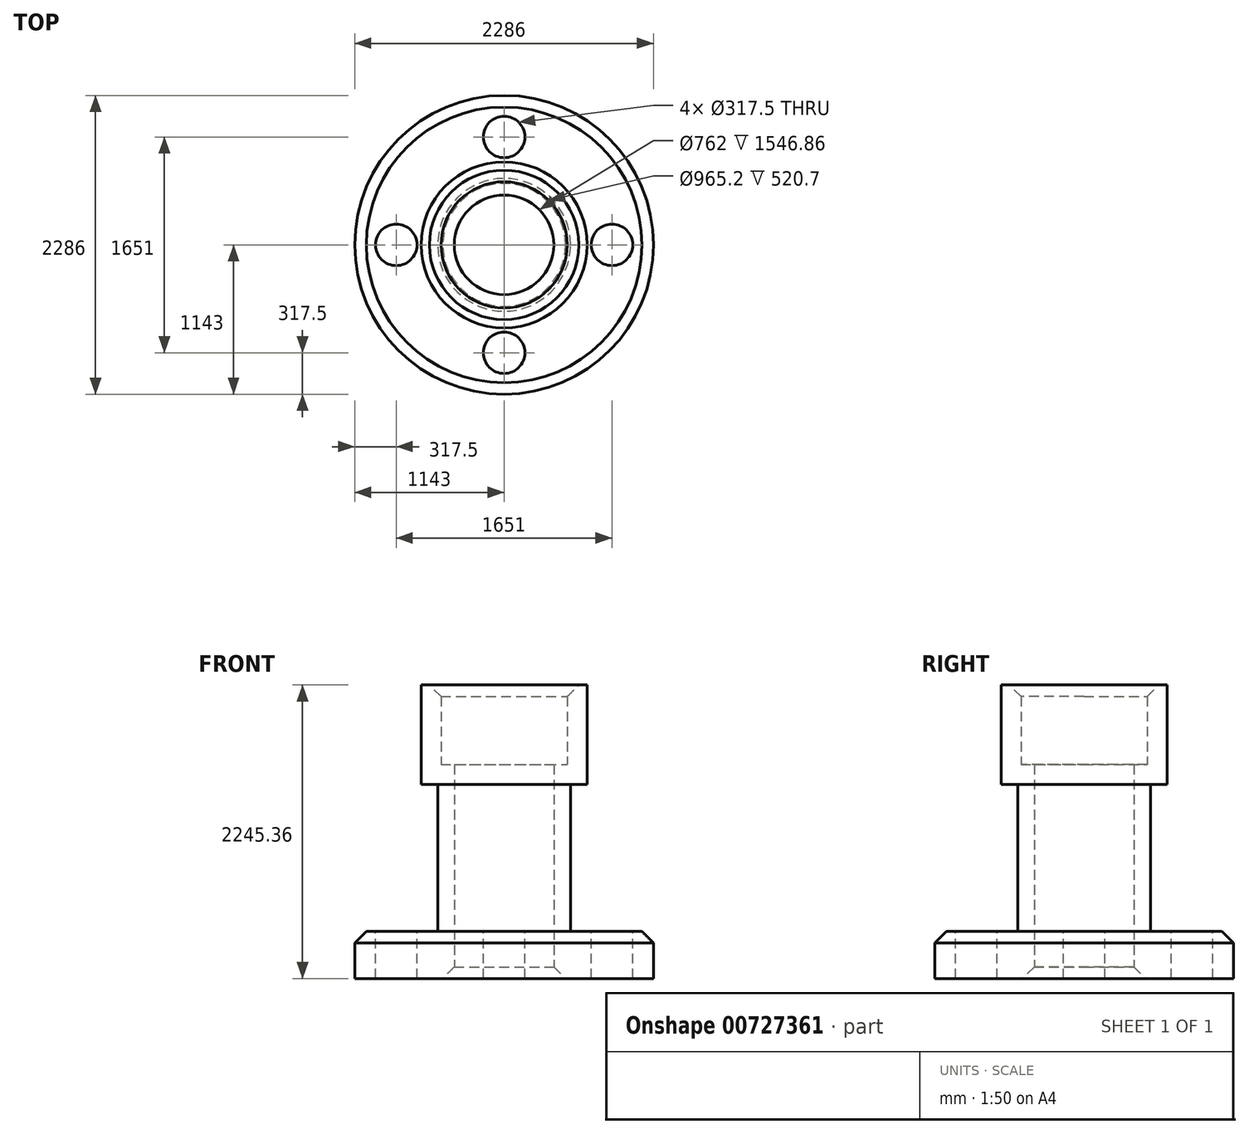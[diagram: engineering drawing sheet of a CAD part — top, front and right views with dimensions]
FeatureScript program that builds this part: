
annotation { "Feature Type Name" : "Feature", "Feature Type Description" : "" }
export const myFeature = defineFeature(function(context is Context, id is Id, definition is map)
    precondition{}
    {
        {
            var Q0;
            Q0=qCreatedBy(makeId("Front.planeOp"),FACE);
            var sketch = newSketch(context, id + "F0", { "sketchPlane" : qUnion([Q0])});
            skLineSegment(sketch, "E0", {"start": v(0, 0) * mm, "end": v(2286, 0) * mm});
            skLineSegment(sketch, "E1", {"start": v(2286, 0) * mm, "end": v(2286, 360.68) * mm});
            skLineSegment(sketch, "E2", {"start": v(1143, 0) * mm, "end": v(1143, 3127.7) * mm});
            skLineSegment(sketch, "E3", {"start": v(2286, 360.68) * mm, "end": v(1651, 360.68) * mm});
            skLineSegment(sketch, "E4", {"start": v(1651, 360.68) * mm, "end": v(1651, 1483.36) * mm});
            skLineSegment(sketch, "E5", {"start": v(1651, 1483.36) * mm, "end": v(1778, 1483.36) * mm});
            skLineSegment(sketch, "E6", {"start": v(1778, 1483.36) * mm, "end": v(1778, 2245.36) * mm});
            skLineSegment(sketch, "E7", {"start": v(1778, 2245.36) * mm, "end": v(1625.6, 2245.36) * mm});
            skLineSegment(sketch, "E8", {"start": v(1625.6, 2245.36) * mm, "end": v(1625.6, 1635.76) * mm});
            skLineSegment(sketch, "E9", {"start": v(1625.6, 1635.76) * mm, "end": v(1524, 1635.76) * mm});
            skLineSegment(sketch, "E10", {"start": v(1524, 1635.76) * mm, "end": v(1524, 0) * mm});
            skSolve(sketch);
        }
        {
            var Q0;
            {var subQ0=sQuery(id+"F0.wireOp",EDGE,"E1");Q0=makeQuery(id+"F0.imprint","IMPRINT",FACE,{"disambiguationData":[TD([[makeQuery(id+"F0.imprint","IMPRINT",EDGE,{"derivedFrom":subQ0}),1.0]])]});}
            var Q1;
            Q1=sQuery(id+"F0.wireOp",EDGE,"E2");
            revolve(context, id + "F1", {"surfaceOperationType" : NewSurfaceOperationType.NEW, "entities" : qUnion([Q0]), "axis" : qUnion([Q1]), "revolveType" : RevolveType.FULL});
        }
        {
            var Q0;
            Q0=makeQuery(id+"F1.opRevolve","SWEPT_EDGE",EDGE,{"disambiguationData":[OSD([sQuery(id+"F0.wireOp",EDGE,"E0"),sQuery(id+"F0.wireOp",EDGE,"E10")])]});
            chamfer(context, id + "F2", {"entities" : qUnion([Q0]), "width" : 88.9 * mm, "tangentPropagation" : true});
        }
        {
            var Q0;
            Q0=makeQuery(id+"F1.opRevolve","SWEPT_EDGE",EDGE,{"disambiguationData":[OSD([sQuery(id+"F0.wireOp",EDGE,"E1"),sQuery(id+"F0.wireOp",EDGE,"E3")])]});
            chamfer(context, id + "F3", {"entities" : qUnion([Q0]), "width" : 88.9 * mm, "tangentPropagation" : true});
        }
        {
            var Q0;
            Q0=makeQuery(id+"F1.opRevolve","SWEPT_EDGE",EDGE,{"disambiguationData":[OSD([sQuery(id+"F0.wireOp",EDGE,"E7"),sQuery(id+"F0.wireOp",EDGE,"E8")])]});
            chamfer(context, id + "F4", {"entities" : qUnion([Q0]), "width" : 88.9 * mm, "tangentPropagation" : true});
        }
        {
            var Q0;
            Q0=makeQuery(id+"F1.opRevolve","SWEPT_FACE",FACE,{"disambiguationData":[OSD([sQuery(id+"F0.wireOp",EDGE,"E3")])]});
            var sketch = newSketch(context, id + "F5", { "sketchPlane" : qUnion([Q0])});
            skCircle(sketch, "E11", {"center": v(1143, 0) * mm, "radius": 825.5 * mm});
            skCircle(sketch, "E12", {"center": v(1143, 825.5) * mm, "radius": 158.75 * mm});
            skCircle(sketch, "E13", {"center": v(1968.5, 0) * mm, "radius": 158.75 * mm});
            skCircle(sketch, "E14", {"center": v(317.5, 0) * mm, "radius": 158.75 * mm});
            skCircle(sketch, "E15", {"center": v(1143, -825.5) * mm, "radius": 158.75 * mm});
            skSolve(sketch);
        }
        {
            var Q0;
            {var subQ0=sQuery(id+"F5.wireOp",EDGE,"E12");var subQ1=sQuery(id+"F5.wireOp",EDGE,"E11");var subQ2=makeQuery(id+"F5.imprint","INTERSECT",VERTEX,{"disambiguationData":[OD(0.0)],"derivedFrom":[subQ1,subQ0]});Q0=makeQuery(id+"F5.imprint","IMPRINT",FACE,{"disambiguationData":[TD([[makeQuery(id+"F5.imprint","IMPRINT",EDGE,{"disambiguationData":[TD([[subQ2,-1.0]])],"derivedFrom":subQ1}),-1.0]])]});}
            var Q1;
            {var subQ0=sQuery(id+"F5.wireOp",EDGE,"E12");var subQ1=sQuery(id+"F5.wireOp",EDGE,"E11");var subQ2=makeQuery(id+"F5.imprint","INTERSECT",VERTEX,{"disambiguationData":[OD(0.0)],"derivedFrom":[subQ1,subQ0]});Q1=makeQuery(id+"F5.imprint","IMPRINT",FACE,{"disambiguationData":[TD([[makeQuery(id+"F5.imprint","IMPRINT",EDGE,{"disambiguationData":[TD([[subQ2,-1.0]])],"derivedFrom":subQ1}),1.0]])]});}
            var Q2;
            {var subQ0=sQuery(id+"F5.wireOp",EDGE,"E13");var subQ1=sQuery(id+"F5.wireOp",EDGE,"E11");var subQ2=makeQuery(id+"F5.imprint","INTERSECT",VERTEX,{"disambiguationData":[OD(0.0)],"derivedFrom":[subQ1,subQ0]});Q2=makeQuery(id+"F5.imprint","IMPRINT",FACE,{"disambiguationData":[TD([[makeQuery(id+"F5.imprint","IMPRINT",EDGE,{"disambiguationData":[TD([[subQ2,1.0]])],"derivedFrom":subQ1}),1.0]])]});}
            var Q3;
            {var subQ0=sQuery(id+"F5.wireOp",EDGE,"E13");var subQ1=sQuery(id+"F5.wireOp",EDGE,"E11");var subQ2=makeQuery(id+"F5.imprint","INTERSECT",VERTEX,{"disambiguationData":[OD(0.0)],"derivedFrom":[subQ1,subQ0]});Q3=makeQuery(id+"F5.imprint","IMPRINT",FACE,{"disambiguationData":[TD([[makeQuery(id+"F5.imprint","IMPRINT",EDGE,{"disambiguationData":[TD([[subQ2,1.0]])],"derivedFrom":subQ1}),-1.0]])]});}
            var Q4;
            {var subQ0=sQuery(id+"F5.wireOp",EDGE,"E15");var subQ1=sQuery(id+"F5.wireOp",EDGE,"E11");var subQ2=makeQuery(id+"F5.imprint","INTERSECT",VERTEX,{"disambiguationData":[OD(0.0)],"derivedFrom":[subQ1,subQ0]});Q4=makeQuery(id+"F5.imprint","IMPRINT",FACE,{"disambiguationData":[TD([[makeQuery(id+"F5.imprint","IMPRINT",EDGE,{"disambiguationData":[TD([[subQ2,-1.0]])],"derivedFrom":subQ1}),1.0]])]});}
            var Q5;
            {var subQ0=sQuery(id+"F5.wireOp",EDGE,"E15");var subQ1=sQuery(id+"F5.wireOp",EDGE,"E11");var subQ2=makeQuery(id+"F5.imprint","INTERSECT",VERTEX,{"disambiguationData":[OD(0.0)],"derivedFrom":[subQ1,subQ0]});Q5=makeQuery(id+"F5.imprint","IMPRINT",FACE,{"disambiguationData":[TD([[makeQuery(id+"F5.imprint","IMPRINT",EDGE,{"disambiguationData":[TD([[subQ2,-1.0]])],"derivedFrom":subQ1}),-1.0]])]});}
            var Q6;
            {var subQ0=sQuery(id+"F5.wireOp",EDGE,"E14");var subQ1=sQuery(id+"F5.wireOp",EDGE,"E11");var subQ2=makeQuery(id+"F5.imprint","INTERSECT",VERTEX,{"disambiguationData":[OD(0.0)],"derivedFrom":[subQ1,subQ0]});Q6=makeQuery(id+"F5.imprint","IMPRINT",FACE,{"disambiguationData":[TD([[makeQuery(id+"F5.imprint","IMPRINT",EDGE,{"disambiguationData":[TD([[subQ2,-1.0]])],"derivedFrom":subQ1}),1.0]])]});}
            var Q7;
            {var subQ0=sQuery(id+"F5.wireOp",EDGE,"E14");var subQ1=sQuery(id+"F5.wireOp",EDGE,"E11");var subQ2=makeQuery(id+"F5.imprint","INTERSECT",VERTEX,{"disambiguationData":[OD(0.0)],"derivedFrom":[subQ1,subQ0]});Q7=makeQuery(id+"F5.imprint","IMPRINT",FACE,{"disambiguationData":[TD([[makeQuery(id+"F5.imprint","IMPRINT",EDGE,{"disambiguationData":[TD([[subQ2,-1.0]])],"derivedFrom":subQ1}),-1.0]])]});}
            extrude(context, id + "F6", {"entities" : qUnion([Q0, Q1, Q2, Q3, Q4, Q5, Q6, Q7]), "operationType" : NewBodyOperationType.REMOVE, "endBound" : BoundingType.THROUGH_ALL, "oppositeDirection" : true, "depth" : 25.4 * mm, "offsetDistance" : 25.4 * mm});
        }
    });
